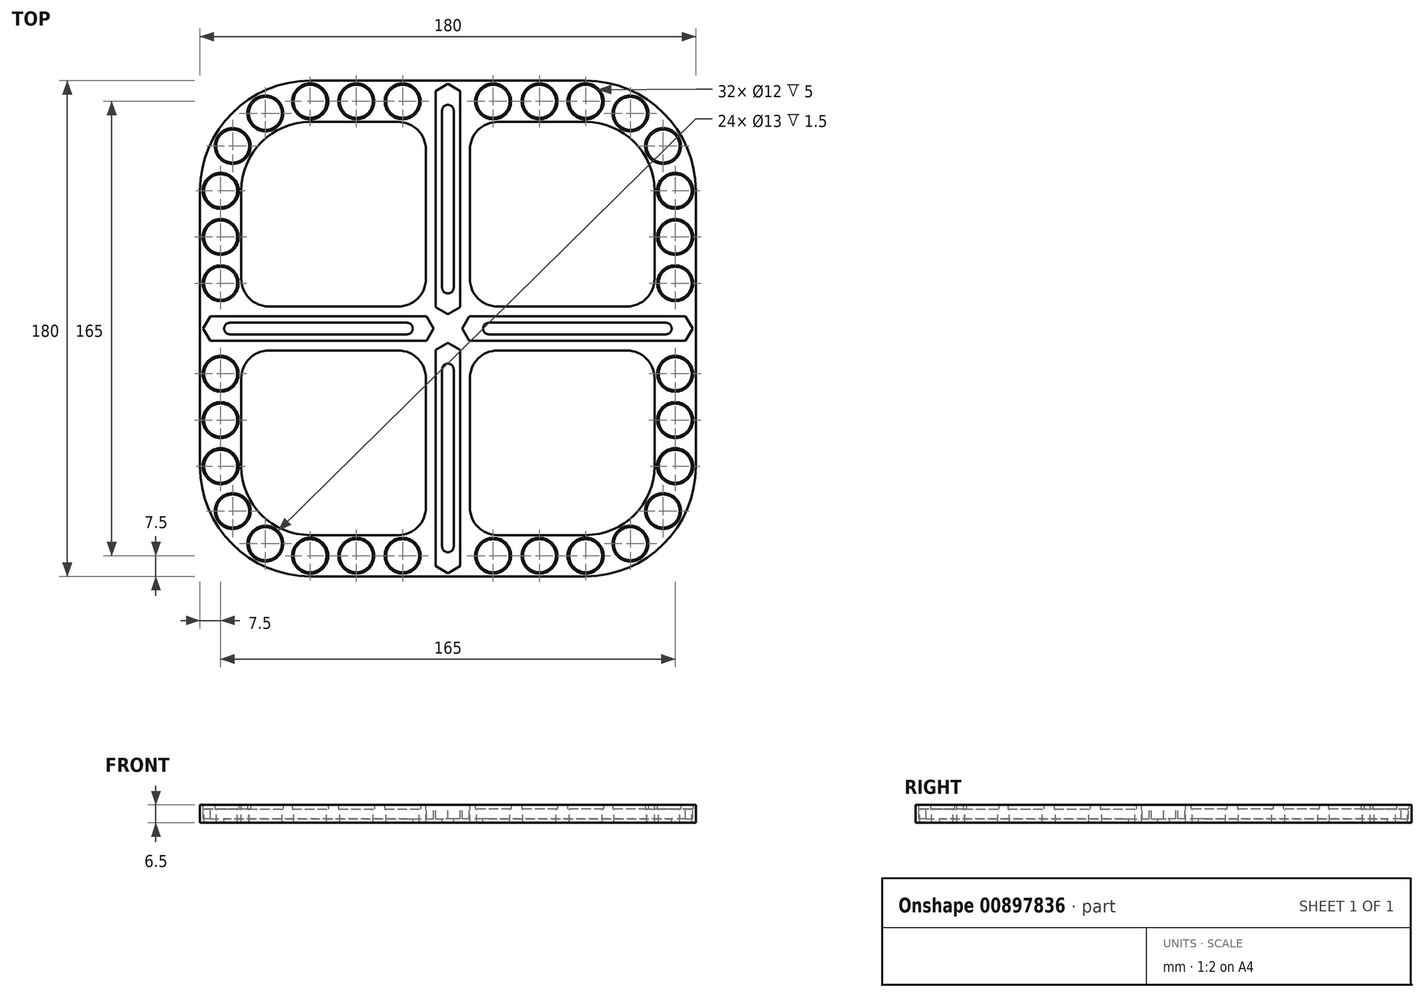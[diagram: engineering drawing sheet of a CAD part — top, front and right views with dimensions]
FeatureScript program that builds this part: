
annotation { "Feature Type Name" : "Feature", "Feature Type Description" : "" }
export const myFeature = defineFeature(function(context is Context, id is Id, definition is map)
    precondition{}
    {
        {
            var Q0;
            Q0=qCreatedBy(makeId("Top.planeOp"),FACE);
            var sketch = newSketch(context, id + "F0", { "sketchPlane" : qUnion([Q0])});
            skLineSegment(sketch, "E0", {"start": v(0, 0) * mm, "end": v(0, -90) * mm, "construction": true});
            skLineSegment(sketch, "E1", {"start": v(0, -90) * mm, "end": v(50, -90) * mm});
            skLineSegment(sketch, "E2", {"start": v(0, 0) * mm, "end": v(8, -8) * mm});
            skArc(sketch, "E3", {"start": v(50, -90) * mm, "mid": v(65.3, -86.96) * mm, "end": v(78.28, -78.28) * mm});
            skLineSegment(sketch, "E4", {"start": v(8, -8) * mm, "end": v(8, -75) * mm});
            skArc(sketch, "E5.0", {"start": v(50, -75) * mm, "mid": v(59.57, -73.1) * mm, "end": v(67.68, -67.68) * mm});
            skLineSegment(sketch, "E5.1", {"start": v(8, -75) * mm, "end": v(50, -75) * mm});
            skLineSegment(sketch, "E6.trimOffspring", {"start": v(67.68, -67.68) * mm, "end": v(78.28, -78.28) * mm, "construction": true});
            skLineSegment(sketch, "E7.MirrorCS", {"start": v(67.68, -67.68) * mm, "end": v(78.28, -78.28) * mm});
            skLineSegment(sketch, "E8", {"start": v(4.5, -86.25) * mm, "end": v(4.5, -7.75) * mm});
            skLineSegment(sketch, "E9.0", {"start": v(4.5, -86.25) * mm, "end": v(0, -88.85) * mm});
            skLineSegment(sketch, "E10", {"start": v(4.5, -7.75) * mm, "end": v(0, -5.15) * mm});
            skLineSegment(sketch, "E11", {"start": v(2.1, -14.85) * mm, "end": v(2.1, -79.15) * mm});
            skArc(sketch, "E12", {"start": v(2.1, -14.85) * mm, "mid": v(1.48, -13.37) * mm, "end": v(0, -12.75) * mm});
            skArc(sketch, "E13", {"start": v(0, -81.25) * mm, "mid": v(1.48, -80.63) * mm, "end": v(2.1, -79.15) * mm});
            skLineSegment(sketch, "E14", {"start": v(0, -81.25) * mm, "end": v(0, -90) * mm});
            skLineSegment(sketch, "E15", {"start": v(0, -12.75) * mm, "end": v(0, 0) * mm});
            skLineSegment(sketch, "E16", {"start": v(8, -75) * mm, "end": v(8, -90) * mm, "construction": true});
            skArc(sketch, "E17.0", {"start": v(50, -82.5) * mm, "mid": v(62.44, -80.03) * mm, "end": v(72.98, -72.98) * mm, "construction": true});
            skLineSegment(sketch, "E17.1", {"start": v(8, -82.5) * mm, "end": v(50, -82.5) * mm, "construction": true});
            skLineSegment(sketch, "E18", {"start": v(8, -82.5) * mm, "end": v(12.3, -82.5) * mm, "construction": true});
            skCircle(sketch, "E19", {"center": v(16.44, -82.5) * mm, "radius": 6 * mm});
            skCircle(sketch, "E20", {"center": v(33.24, -82.5) * mm, "radius": 6 * mm});
            skCircle(sketch, "E21", {"center": v(50.03, -82.5) * mm, "radius": 6 * mm});
            skCircle(sketch, "E22", {"center": v(66.26, -78.14) * mm, "radius": 6 * mm});
            skCircle(sketch, "E23", {"center": v(16.44, -82.5) * mm, "radius": 7.5 * mm});
            skCircle(sketch, "E24", {"center": v(33.24, -82.5) * mm, "radius": 7.5 * mm});
            skCircle(sketch, "E25", {"center": v(50, -82.5) * mm, "radius": 7.5 * mm});
            skCircle(sketch, "E26", {"center": v(66.26, -78.14) * mm, "radius": 7.5 * mm});
            skCircle(sketch, "E27", {"center": v(16.44, -82.5) * mm, "radius": 6.5 * mm});
            skCircle(sketch, "E28", {"center": v(33.24, -82.5) * mm, "radius": 6.5 * mm});
            skCircle(sketch, "E29", {"center": v(50, -82.5) * mm, "radius": 6.54 * mm});
            skCircle(sketch, "E30", {"center": v(66.26, -78.14) * mm, "radius": 6.5 * mm});
            skLineSegment(sketch, "E31.0", {"start": v(9.46, -9.46) * mm, "end": v(0, -4) * mm});
            skLineSegment(sketch, "E31.1", {"start": v(5.5, -86.82) * mm, "end": v(5.5, -5.65) * mm});
            skLineSegment(sketch, "E31.2", {"start": v(5.5, -86.82) * mm, "end": v(0, -90) * mm});
            skSolve(sketch);
        }
        {
            var Q0;
            {var subQ0=sQuery(id+"F0.wireOp",EDGE,"E23");var subQ1=sQuery(id+"F0.wireOp",EDGE,"E1");var subQ2=makeQuery(id+"F0.imprint","INTERSECT",VERTEX,{"derivedFrom":[subQ1,subQ0]});Q0=makeQuery(id+"F0.imprint","IMPRINT",FACE,{"disambiguationData":[TD([[makeQuery(id+"F0.imprint","IMPRINT",EDGE,{"disambiguationData":[TD([[subQ2,-1.0]])],"derivedFrom":subQ1}),1.0]])]});}
            var Q1;
            Q1=makeQuery(id+"F0.imprint","IMPRINT",FACE,{"disambiguationData":[TD([[makeQuery(id+"F0.imprint","IMPRINT",EDGE,{"derivedFrom":sQuery(id+"F0.wireOp",EDGE,"E8")}),1.0]])]});
            var Q2;
            Q2=makeQuery(id+"F0.imprint","IMPRINT",FACE,{"disambiguationData":[TD([[makeQuery(id+"F0.imprint","IMPRINT",EDGE,{"derivedFrom":sQuery(id+"F0.wireOp",EDGE,"E19")}),-1.0]])]});
            var Q3;
            Q3=makeQuery(id+"F0.imprint","IMPRINT",FACE,{"disambiguationData":[TD([[makeQuery(id+"F0.imprint","IMPRINT",EDGE,{"derivedFrom":sQuery(id+"F0.wireOp",EDGE,"E20")}),-1.0]])]});
            var Q4;
            {var subQ1=sQuery(id+"F0.wireOp",EDGE,"E1");var subQ3=sQuery(id+"F0.wireOp",EDGE,"E24");var subQ4=makeQuery(id+"F0.imprint","INTERSECT",VERTEX,{"derivedFrom":[subQ1,subQ3]});Q4=makeQuery(id+"F0.imprint","IMPRINT",FACE,{"disambiguationData":[TD([[makeQuery(id+"F0.imprint","IMPRINT",EDGE,{"disambiguationData":[TD([[subQ4,-1.0]])],"derivedFrom":subQ3}),-1.0]])]});}
            var Q5;
            Q5=makeQuery(id+"F0.imprint","IMPRINT",FACE,{"disambiguationData":[TD([[makeQuery(id+"F0.imprint","IMPRINT",EDGE,{"derivedFrom":sQuery(id+"F0.wireOp",EDGE,"E21")}),-1.0]])]});
            var Q6;
            {var subQ1=sQuery(id+"F0.wireOp",EDGE,"E3");var subQ3=sQuery(id+"F0.wireOp",EDGE,"E26");var subQ4=makeQuery(id+"F0.imprint","INTERSECT",VERTEX,{"derivedFrom":[subQ1,subQ3]});Q6=makeQuery(id+"F0.imprint","IMPRINT",FACE,{"disambiguationData":[TD([[makeQuery(id+"F0.imprint","IMPRINT",EDGE,{"disambiguationData":[TD([[subQ4,1.0]])],"derivedFrom":subQ3}),-1.0]])]});}
            var Q7;
            Q7=makeQuery(id+"F0.imprint","IMPRINT",FACE,{"disambiguationData":[TD([[makeQuery(id+"F0.imprint","IMPRINT",EDGE,{"derivedFrom":sQuery(id+"F0.wireOp",EDGE,"E22")}),-1.0]])]});
            var Q8;
            {var subQ0=sQuery(id+"F0.wireOp",EDGE,"E7.MirrorCS");Q8=makeQuery(id+"F0.imprint","IMPRINT",FACE,{"disambiguationData":[TD([[makeQuery(id+"F0.imprint","IMPRINT",EDGE,{"derivedFrom":subQ0}),-1.0]])]});}
            var Q9;
            {var subQ0=sQuery(id+"F0.wireOp",EDGE,"t1Ie4vdN-QEID-KtYz-A2sY-hLR0Ntny4cb7");Q9=makeQuery(id+"F0.imprint","IMPRINT",FACE,{"disambiguationData":[TD([[makeQuery(id+"F0.imprint","IMPRINT",EDGE,{"derivedFrom":subQ0}),1.0]])]});}
            var Q10;
            {var subQ3=sQuery(id+"F0.wireOp",EDGE,"SWZi8AJM-BAiN-23Z5-PYL8-0rGgskA9mhrW");Q10=makeQuery(id+"F0.imprint","IMPRINT",FACE,{"disambiguationData":[TD([[makeQuery(id+"F0.imprint","IMPRINT",EDGE,{"derivedFrom":subQ3}),1.0]])]});}
            var Q11;
            {var subQ5=sQuery(id+"F0.wireOp",EDGE,"E4");Q11=makeQuery(id+"F0.imprint","IMPRINT",FACE,{"disambiguationData":[TD([[makeQuery(id+"F0.imprint","IMPRINT",EDGE,{"derivedFrom":subQ5}),-1.0]])]});}
            var Q12;
            Q12=makeQuery(id+"F0.imprint","IMPRINT",FACE,{"disambiguationData":[TD([[makeQuery(id+"F0.imprint","IMPRINT",EDGE,{"derivedFrom":sQuery(id+"F0.wireOp",EDGE,"E28")}),-1.0]])]});
            var Q13;
            Q13=makeQuery(id+"F0.imprint","IMPRINT",FACE,{"disambiguationData":[TD([[makeQuery(id+"F0.imprint","IMPRINT",EDGE,{"derivedFrom":sQuery(id+"F0.wireOp",EDGE,"E29")}),-1.0]])]});
            var Q14;
            Q14=makeQuery(id+"F0.imprint","IMPRINT",FACE,{"disambiguationData":[TD([[makeQuery(id+"F0.imprint","IMPRINT",EDGE,{"derivedFrom":sQuery(id+"F0.wireOp",EDGE,"E30")}),-1.0]])]});
            var Q15;
            Q15=makeQuery(id+"F0.imprint","IMPRINT",FACE,{"disambiguationData":[TD([[makeQuery(id+"F0.imprint","IMPRINT",EDGE,{"derivedFrom":sQuery(id+"F0.wireOp",EDGE,"E27")}),-1.0]])]});
            var Q16;
            Q16=makeQuery(id+"F0.imprint","IMPRINT",FACE,{"disambiguationData":[TD([[makeQuery(id+"F0.imprint","IMPRINT",EDGE,{"derivedFrom":sQuery(id+"F0.wireOp",EDGE,"E8")}),-1.0]])]});
            var Q17;
            {var subQ3=sQuery(id+"F0.wireOp",EDGE,"E31.0");Q17=makeQuery(id+"F0.imprint","IMPRINT",FACE,{"disambiguationData":[TD([[makeQuery(id+"F0.imprint","IMPRINT",EDGE,{"derivedFrom":subQ3}),-1.0]])]});}
            var Q18;
            {var subQ5=sQuery(id+"F0.wireOp",EDGE,"E31.2");Q18=makeQuery(id+"F0.imprint","IMPRINT",FACE,{"disambiguationData":[TD([[makeQuery(id+"F0.imprint","IMPRINT",EDGE,{"derivedFrom":subQ5}),1.0]])]});}
            extrude(context, id + "F1", {"entities" : qUnion([Q0, Q1, Q2, Q3, Q4, Q5, Q6, Q7, Q8, Q9, Q10, Q11, Q12, Q13, Q14, Q15, Q16, Q17, Q18]), "oppositeDirection" : true, "depth" : 5 * mm, "offsetDistance" : 25 * mm});
        }
        {
            var Q0;
            Q0=makeQuery(id+"F0.imprint","IMPRINT",FACE,{"disambiguationData":[TD([[makeQuery(id+"F0.imprint","IMPRINT",EDGE,{"derivedFrom":sQuery(id+"F0.wireOp",EDGE,"E8")}),1.0]])]});
            extrude(context, id + "F2", {"entities" : qUnion([Q0]), "operationType" : NewBodyOperationType.REMOVE, "oppositeDirection" : true, "depth" : 3.5 * mm, "offsetDistance" : 25 * mm});
        }
        {
            var Q0;
            Q0=makeQuery(id+"F0.imprint","IMPRINT",FACE,{"disambiguationData":[TD([[makeQuery(id+"F0.imprint","IMPRINT",EDGE,{"derivedFrom":sQuery(id+"F0.wireOp",EDGE,"E27")}),-1.0]])]});
            var Q1;
            Q1=makeQuery(id+"F0.imprint","IMPRINT",FACE,{"disambiguationData":[TD([[makeQuery(id+"F0.imprint","IMPRINT",EDGE,{"derivedFrom":sQuery(id+"F0.wireOp",EDGE,"E28")}),-1.0]])]});
            var Q2;
            Q2=makeQuery(id+"F0.imprint","IMPRINT",FACE,{"disambiguationData":[TD([[makeQuery(id+"F0.imprint","IMPRINT",EDGE,{"derivedFrom":sQuery(id+"F0.wireOp",EDGE,"E29")}),-1.0]])]});
            var Q3;
            Q3=makeQuery(id+"F0.imprint","IMPRINT",FACE,{"disambiguationData":[TD([[makeQuery(id+"F0.imprint","IMPRINT",EDGE,{"derivedFrom":sQuery(id+"F0.wireOp",EDGE,"E30")}),-1.0]])]});
            var Q4;
            {var subQ0=sQuery(id+"F0.wireOp",EDGE,"t1Ie4vdN-QEID-KtYz-A2sY-hLR0Ntny4cb7");Q4=makeQuery(id+"F0.imprint","IMPRINT",FACE,{"disambiguationData":[TD([[makeQuery(id+"F0.imprint","IMPRINT",EDGE,{"derivedFrom":subQ0}),1.0]])]});}
            var Q5;
            Q5=makeQuery(id+"F0.imprint","IMPRINT",FACE,{"disambiguationData":[TD([[makeQuery(id+"F0.imprint","IMPRINT",EDGE,{"derivedFrom":sQuery(id+"F0.wireOp",EDGE,"E8")}),-1.0]])]});
            var Q6;
            {var subQ5=sQuery(id+"F0.wireOp",EDGE,"E31.2");Q6=makeQuery(id+"F0.imprint","IMPRINT",FACE,{"disambiguationData":[TD([[makeQuery(id+"F0.imprint","IMPRINT",EDGE,{"derivedFrom":subQ5}),1.0]])]});}
            var Q7;
            {var subQ0=sQuery(id+"F0.wireOp",EDGE,"E23");var subQ1=sQuery(id+"F0.wireOp",EDGE,"E1");var subQ2=makeQuery(id+"F0.imprint","INTERSECT",VERTEX,{"derivedFrom":[subQ1,subQ0]});Q7=makeQuery(id+"F0.imprint","IMPRINT",FACE,{"disambiguationData":[TD([[makeQuery(id+"F0.imprint","IMPRINT",EDGE,{"disambiguationData":[TD([[subQ2,-1.0]])],"derivedFrom":subQ1}),1.0]])]});}
            var Q8;
            {var subQ1=sQuery(id+"F0.wireOp",EDGE,"E1");var subQ3=sQuery(id+"F0.wireOp",EDGE,"E24");var subQ4=makeQuery(id+"F0.imprint","INTERSECT",VERTEX,{"derivedFrom":[subQ1,subQ3]});Q8=makeQuery(id+"F0.imprint","IMPRINT",FACE,{"disambiguationData":[TD([[makeQuery(id+"F0.imprint","IMPRINT",EDGE,{"disambiguationData":[TD([[subQ4,-1.0]])],"derivedFrom":subQ3}),-1.0]])]});}
            var Q9;
            {var subQ1=sQuery(id+"F0.wireOp",EDGE,"E3");var subQ3=sQuery(id+"F0.wireOp",EDGE,"E26");var subQ4=makeQuery(id+"F0.imprint","INTERSECT",VERTEX,{"derivedFrom":[subQ1,subQ3]});Q9=makeQuery(id+"F0.imprint","IMPRINT",FACE,{"disambiguationData":[TD([[makeQuery(id+"F0.imprint","IMPRINT",EDGE,{"disambiguationData":[TD([[subQ4,1.0]])],"derivedFrom":subQ3}),-1.0]])]});}
            var Q10;
            {var subQ0=sQuery(id+"F0.wireOp",EDGE,"E7.MirrorCS");Q10=makeQuery(id+"F0.imprint","IMPRINT",FACE,{"disambiguationData":[TD([[makeQuery(id+"F0.imprint","IMPRINT",EDGE,{"derivedFrom":subQ0}),-1.0]])]});}
            var Q11;
            {var subQ0=sQuery(id+"F0.wireOp",EDGE,"E15");var subQ1=sQuery(id+"F0.wireOp",EDGE,"E2");var subQ2=makeQuery(id+"F0.imprint","INTERSECT",VERTEX,{"derivedFrom":[subQ1,subQ0]});Q11=makeQuery(id+"F0.imprint","IMPRINT",FACE,{"disambiguationData":[TD([[makeQuery(id+"F0.imprint","IMPRINT",EDGE,{"disambiguationData":[TD([[subQ2,-1.0]])],"derivedFrom":subQ1}),-1.0]])]});}
            var Q12;
            {var subQ0=sQuery(id+"F0.wireOp",EDGE,"E4");var subQ1=sQuery(id+"F0.wireOp",EDGE,"E2");var subQ2=makeQuery(id+"F0.imprint","INTERSECT",VERTEX,{"derivedFrom":[subQ1,subQ0]});Q12=makeQuery(id+"F0.imprint","IMPRINT",FACE,{"disambiguationData":[TD([[makeQuery(id+"F0.imprint","IMPRINT",EDGE,{"disambiguationData":[TD([[subQ2,1.0]])],"derivedFrom":subQ1}),-1.0]])]});}
            extrude(context, id + "F3", {"entities" : qUnion([Q0, Q1, Q2, Q3, Q4, Q5, Q6, Q7, Q8, Q9, Q10, Q11, Q12]), "operationType" : NewBodyOperationType.ADD, "depth" : 1.5 * mm, "offsetDistance" : 25 * mm});
        }
        {
            var Q0;
            Q0=makeQuery(id+"F1.opExtrude","SWEPT_BODY",BODY,{"disambiguationData":[OSD([sQuery(id+"F0.wireOp",EDGE,"E1"),sQuery(id+"F0.wireOp",EDGE,"E2"),sQuery(id+"F0.wireOp",EDGE,"E3"),sQuery(id+"F0.wireOp",EDGE,"E4"),sQuery(id+"F0.wireOp",EDGE,"E5.0"),sQuery(id+"F0.wireOp",EDGE,"E5.1"),sQuery(id+"F0.wireOp",EDGE,"E7.MirrorCS"),sQuery(id+"F0.wireOp",EDGE,"E11"),sQuery(id+"F0.wireOp",EDGE,"E12"),sQuery(id+"F0.wireOp",EDGE,"E13"),sQuery(id+"F0.wireOp",EDGE,"E14"),sQuery(id+"F0.wireOp",EDGE,"E15"),sQuery(id+"F0.wireOp",EDGE,"E19"),sQuery(id+"F0.wireOp",EDGE,"E20"),sQuery(id+"F0.wireOp",EDGE,"E21"),sQuery(id+"F0.wireOp",EDGE,"E22")])]});
            var Q1;
            Q1=makeQuery(id+"F1.opExtrude","SWEPT_FACE",FACE,{"disambiguationData":[OSD([sQuery(id+"F0.wireOp",EDGE,"E2")])]});
            mirror(context, id + "F4", {"operationType" : NewBodyOperationType.ADD, "entities" : qUnion([Q0]), "mirrorPlane" : qUnion([Q1])});
        }
        {
            var Q0;
            {var subQ0=makeQuery(id+"F1.opExtrude","SWEPT_EDGE",EDGE,{"disambiguationData":[OSD([sQuery(id+"F0.wireOp",EDGE,"E2"),sQuery(id+"F0.wireOp",EDGE,"E4")])]});Q0=makeQuery(id+"F4.boolean.opBoolean","MERGE",EDGE,{"derivedFrom":[subQ0,makeQuery(id+"F4.opPattern","COPY",EDGE,{"derivedFrom":subQ0,"instanceName":"1"})]});}
            var Q1;
            Q1=makeQuery(id+"F4.opPattern","COPY",EDGE,{"derivedFrom":makeQuery(id+"F1.opExtrude","SWEPT_EDGE",EDGE,{"disambiguationData":[OSD([sQuery(id+"F0.wireOp",EDGE,"E4"),sQuery(id+"F0.wireOp",EDGE,"E5.1")])]}),"instanceName":"1"});
            var Q2;
            Q2=makeQuery(id+"F1.opExtrude","SWEPT_EDGE",EDGE,{"disambiguationData":[OSD([sQuery(id+"F0.wireOp",EDGE,"E4"),sQuery(id+"F0.wireOp",EDGE,"E5.1")])]});
            fillet(context, id + "F5", {"entities" : qUnion([Q0, Q1, Q2]), "radius" : 10 * mm, "tangentPropagation" : true, "allowEdgeOverflow" : false});
        }
        {
            var Q0;
            Q0=makeQuery(id+"F1.opExtrude","SWEPT_BODY",BODY,{"disambiguationData":[OSD([sQuery(id+"F0.wireOp",EDGE,"E1"),sQuery(id+"F0.wireOp",EDGE,"E2"),sQuery(id+"F0.wireOp",EDGE,"E3"),sQuery(id+"F0.wireOp",EDGE,"E4"),sQuery(id+"F0.wireOp",EDGE,"E5.0"),sQuery(id+"F0.wireOp",EDGE,"E5.1"),sQuery(id+"F0.wireOp",EDGE,"E7.MirrorCS"),sQuery(id+"F0.wireOp",EDGE,"E11"),sQuery(id+"F0.wireOp",EDGE,"E12"),sQuery(id+"F0.wireOp",EDGE,"E13"),sQuery(id+"F0.wireOp",EDGE,"E14"),sQuery(id+"F0.wireOp",EDGE,"E15")])]});
            var Q1;
            {var subQ0=makeQuery(id+"F1.opExtrude","SWEPT_EDGE",EDGE,{"disambiguationData":[OSD([sQuery(id+"F0.wireOp",EDGE,"E2"),sQuery(id+"F0.wireOp",EDGE,"E15")])]});Q1=makeQuery(id+"F4.boolean.opBoolean","MERGE",EDGE,{"derivedFrom":[subQ0,makeQuery(id+"F4.opPattern","COPY",EDGE,{"derivedFrom":subQ0,"instanceName":"1"})]});}
            circularPattern(context, id + "F6", {"operationType" : NewBodyOperationType.ADD, "entities" : qUnion([Q0]), "axis" : qUnion([Q1]), "angle" : 360 * degree, "instanceCount" : 4, "equalSpace" : true});
        }
    });
